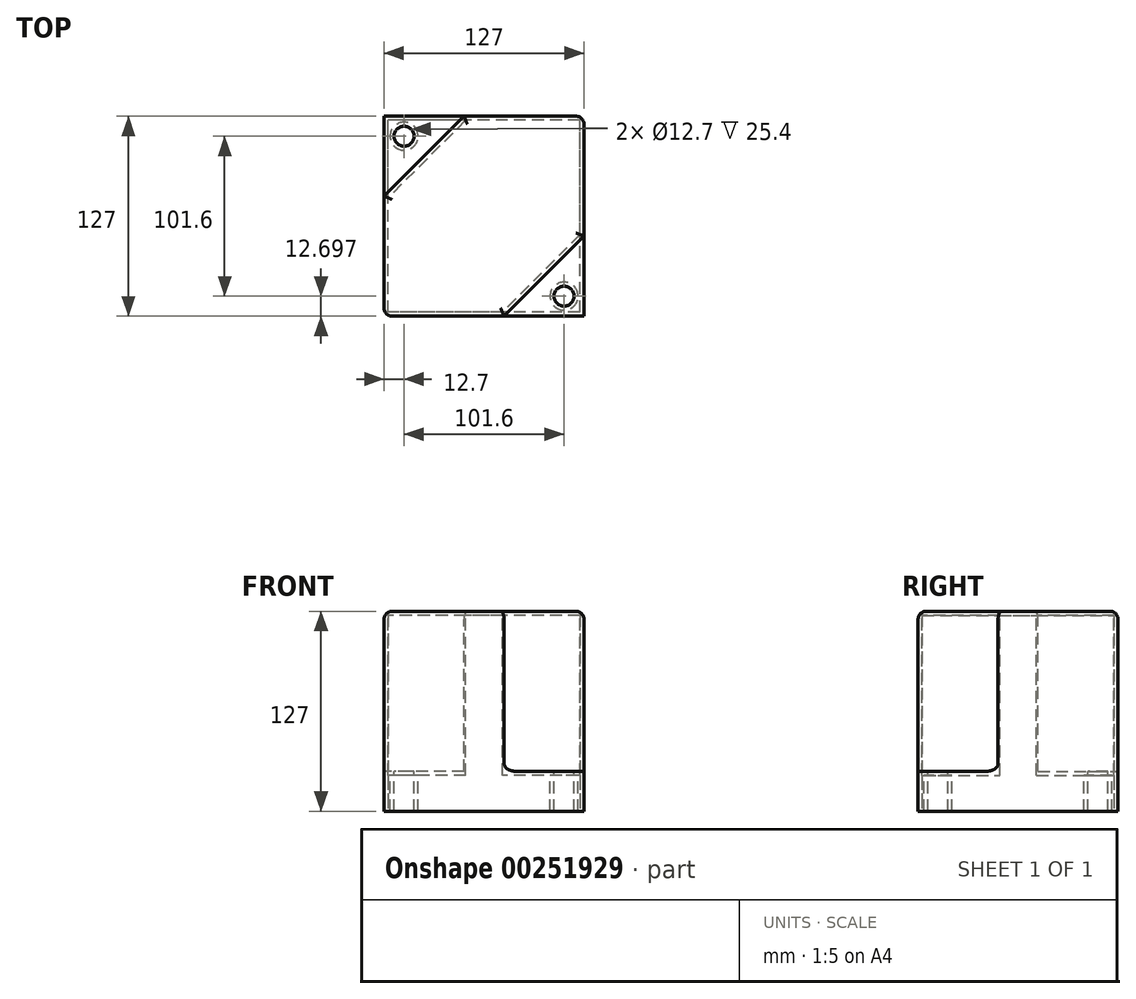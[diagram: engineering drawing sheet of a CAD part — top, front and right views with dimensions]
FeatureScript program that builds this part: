
annotation { "Feature Type Name" : "Feature", "Feature Type Description" : "" }
export const myFeature = defineFeature(function(context is Context, id is Id, definition is map)
    precondition{}
    {
        {
            var Q0;
            Q0=qCreatedBy(makeId("Top.planeOp"),FACE);
            var sketch = newSketch(context, id + "F0", { "sketchPlane" : qUnion([Q0])});
            skLineSegment(sketch, "E0.bottom", {"start": v(63.5, -63.6) * mm, "end": v(-63.5, -63.6) * mm});
            skLineSegment(sketch, "E0.top", {"start": v(63.5, 63.4) * mm, "end": v(-63.5, 63.4) * mm});
            skLineSegment(sketch, "E0.left", {"start": v(63.5, -63.6) * mm, "end": v(63.5, 63.4) * mm});
            skLineSegment(sketch, "E0.right", {"start": v(-63.5, -63.6) * mm, "end": v(-63.5, 63.4) * mm});
            skPoint(sketch, "E0.middle", {"position": v(0, -0.1) * mm});
            skSolve(sketch);
        }
        {
            var Q0;
            Q0 = qSketchRegion(id + "F0", true);
            extrude(context, id + "F1", {"entities" : qUnion([Q0]), "depth" : 127 * mm});
        }
        {
            var Q0;
            Q0=makeQuery(id+"F1.opExtrude","CAP_FACE",FACE,{"disambiguationData":[OSD([sQuery(id+"F0.wireOp",EDGE,"E0.bottom"),sQuery(id+"F0.wireOp",EDGE,"E0.top"),sQuery(id+"F0.wireOp",EDGE,"E0.left"),sQuery(id+"F0.wireOp",EDGE,"E0.right")])],"isStart":false});
            var sketch = newSketch(context, id + "F2", { "sketchPlane" : qUnion([Q0])});
            skLineSegment(sketch, "E1", {"start": v(-63.5, 63.4) * mm, "end": v(-12.7, 63.4) * mm});
            skLineSegment(sketch, "E2", {"start": v(-12.7, 63.4) * mm, "end": v(-63.5, 12.6) * mm});
            skLineSegment(sketch, "E3", {"start": v(-63.5, 12.6) * mm, "end": v(-63.5, 63.4) * mm});
            skLineSegment(sketch, "E4", {"start": v(63.5, -63.6) * mm, "end": v(63.5, -12.8) * mm});
            skLineSegment(sketch, "E5", {"start": v(63.5, -12.8) * mm, "end": v(12.7, -63.6) * mm});
            skLineSegment(sketch, "E6", {"start": v(12.7, -63.6) * mm, "end": v(63.5, -63.6) * mm});
            skSolve(sketch);
        }
        {
            var Q0;
            Q0=makeQuery(id+"F2.imprint","IMPRINT",FACE,{"disambiguationData":[TD([[makeQuery(id+"F2.imprint","IMPRINT",EDGE,{"derivedFrom":sQuery(id+"F2.wireOp",EDGE,"E1")}),1.0]])]});
            var Q1;
            Q1=makeQuery(id+"F2.imprint","IMPRINT",FACE,{"disambiguationData":[TD([[makeQuery(id+"F2.imprint","IMPRINT",EDGE,{"derivedFrom":sQuery(id+"F2.wireOp",EDGE,"E4")}),1.0]])]});
            extrude(context, id + "F3", {"entities" : qUnion([Q0, Q1]), "operationType" : NewBodyOperationType.REMOVE, "oppositeDirection" : true, "depth" : 101.6 * mm});
        }
        {
            var Q0;
            Q0=makeQuery(id+"F1.opExtrude","CAP_FACE",FACE,{"disambiguationData":[OSD([sQuery(id+"F0.wireOp",EDGE,"E0.bottom"),sQuery(id+"F0.wireOp",EDGE,"E0.top"),sQuery(id+"F0.wireOp",EDGE,"E0.left"),sQuery(id+"F0.wireOp",EDGE,"E0.right")])],"isStart":false});
            var sketch = newSketch(context, id + "F4", { "sketchPlane" : qUnion([Q0])});
            skCircle(sketch, "E7", {"center": v(-50.8, 50.7) * mm, "radius": 6.35 * mm});
            skCircle(sketch, "E8", {"center": v(50.8, -50.9) * mm, "radius": 6.35 * mm});
            skSolve(sketch);
        }
        {
            var Q0;
            Q0=makeQuery(id+"F4.imprint","IMPRINT",FACE,{"disambiguationData":[TD([[makeQuery(id+"F4.imprint","IMPRINT",EDGE,{"derivedFrom":sQuery(id+"F4.wireOp",EDGE,"E7")}),1.0]])]});
            var Q1;
            Q1=makeQuery(id+"F4.imprint","IMPRINT",FACE,{"disambiguationData":[TD([[makeQuery(id+"F4.imprint","IMPRINT",EDGE,{"derivedFrom":sQuery(id+"F4.wireOp",EDGE,"E8")}),1.0]])]});
            extrude(context, id + "F5", {"entities" : qUnion([Q0, Q1]), "operationType" : NewBodyOperationType.REMOVE, "oppositeDirection" : true, "depth" : 203.2 * mm});
        }
        {
            var Q0;
            Q0=makeQuery(id+"F1.opExtrude","CAP_FACE",FACE,{"disambiguationData":[OSD([sQuery(id+"F0.wireOp",EDGE,"E0.bottom"),sQuery(id+"F0.wireOp",EDGE,"E0.top"),sQuery(id+"F0.wireOp",EDGE,"E0.left"),sQuery(id+"F0.wireOp",EDGE,"E0.right")])],"isStart":true});
            shell(context, id + "F6", {"entities" : qUnion([Q0]), "thickness" : 2.54 * mm});
        }
        {
            var Q0;
            Q0=makeQuery(id+"F3.boolean.opBoolean","COPY",EDGE,{"derivedFrom":makeQuery(id+"F3.opExtrude","CAP_EDGE",EDGE,{"disambiguationData":[OSD([sQuery(id+"F2.wireOp",EDGE,"E5")])],"isStart":true})});
            var Q1;
            Q1=makeQuery(id+"F1.opExtrude","CAP_EDGE",EDGE,{"disambiguationData":[OSD([sQuery(id+"F0.wireOp",EDGE,"E0.bottom")])],"isStart":false});
            var Q2;
            Q2=makeQuery(id+"F1.opExtrude","CAP_EDGE",EDGE,{"disambiguationData":[OSD([sQuery(id+"F0.wireOp",EDGE,"E0.right")])],"isStart":false});
            var Q3;
            Q3=makeQuery(id+"F1.opExtrude","CAP_FACE",FACE,{"disambiguationData":[OSD([sQuery(id+"F0.wireOp",EDGE,"E0.bottom"),sQuery(id+"F0.wireOp",EDGE,"E0.top"),sQuery(id+"F0.wireOp",EDGE,"E0.left"),sQuery(id+"F0.wireOp",EDGE,"E0.right")])],"isStart":false});
            var Q4;
            Q4=makeQuery(id+"F3.boolean.opBoolean","COPY",EDGE,{"derivedFrom":makeQuery(id+"F3.opExtrude","SWEPT_EDGE",EDGE,{"disambiguationData":[OSD([sQuery(id+"F0.wireOp",EDGE,"E0.left"),sQuery(id+"F2.wireOp",EDGE,"E4"),sQuery(id+"F2.wireOp",EDGE,"E5")])]})});
            var Q5;
            Q5=makeQuery(id+"F3.boolean.opBoolean","COPY",EDGE,{"derivedFrom":makeQuery(id+"F3.opExtrude","SWEPT_EDGE",EDGE,{"disambiguationData":[OSD([sQuery(id+"F0.wireOp",EDGE,"E0.bottom"),sQuery(id+"F2.wireOp",EDGE,"E5"),sQuery(id+"F2.wireOp",EDGE,"E6")])]})});
            var Q6;
            Q6=makeQuery(id+"F3.boolean.opBoolean","COPY",EDGE,{"derivedFrom":makeQuery(id+"F3.opExtrude","CAP_EDGE",EDGE,{"disambiguationData":[OSD([sQuery(id+"F2.wireOp",EDGE,"E6")])],"isStart":false})});
            var Q7;
            Q7=makeQuery(id+"F3.boolean.opBoolean","COPY",EDGE,{"derivedFrom":makeQuery(id+"F3.opExtrude","CAP_EDGE",EDGE,{"disambiguationData":[OSD([sQuery(id+"F2.wireOp",EDGE,"E4")])],"isStart":false})});
            var Q8;
            Q8=makeQuery(id+"F3.boolean.opBoolean","COPY",EDGE,{"derivedFrom":makeQuery(id+"F3.opExtrude","CAP_EDGE",EDGE,{"disambiguationData":[OSD([sQuery(id+"F2.wireOp",EDGE,"E5")])],"isStart":false})});
            var Q9;
            Q9=makeQuery(id+"F1.opExtrude","SWEPT_EDGE",EDGE,{"disambiguationData":[OSD([sQuery(id+"F0.wireOp",EDGE,"E0.top"),sQuery(id+"F0.wireOp",EDGE,"E0.left")])]});
            var Q10;
            Q10=makeQuery(id+"F1.opExtrude","SWEPT_EDGE",EDGE,{"disambiguationData":[OSD([sQuery(id+"F0.wireOp",EDGE,"E0.bottom"),sQuery(id+"F0.wireOp",EDGE,"E0.right")])]});
            var Q11;
            Q11=makeQuery(id+"F3.boolean.opBoolean","COPY",EDGE,{"derivedFrom":makeQuery(id+"F3.opExtrude","SWEPT_EDGE",EDGE,{"disambiguationData":[OSD([sQuery(id+"F0.wireOp",EDGE,"E0.top"),sQuery(id+"F2.wireOp",EDGE,"E1"),sQuery(id+"F2.wireOp",EDGE,"E2")])]})});
            var Q12;
            Q12=makeQuery(id+"F3.boolean.opBoolean","COPY",EDGE,{"derivedFrom":makeQuery(id+"F3.opExtrude","SWEPT_EDGE",EDGE,{"disambiguationData":[OSD([sQuery(id+"F0.wireOp",EDGE,"E0.right"),sQuery(id+"F2.wireOp",EDGE,"E2"),sQuery(id+"F2.wireOp",EDGE,"E3")])]})});
            var Q13;
            Q13=makeQuery(id+"F3.boolean.opBoolean","COPY",EDGE,{"derivedFrom":makeQuery(id+"F3.opExtrude","CAP_EDGE",EDGE,{"disambiguationData":[OSD([sQuery(id+"F2.wireOp",EDGE,"E3")])],"isStart":false})});
            var Q14;
            Q14=makeQuery(id+"F3.boolean.opBoolean","COPY",EDGE,{"derivedFrom":makeQuery(id+"F3.opExtrude","CAP_EDGE",EDGE,{"disambiguationData":[OSD([sQuery(id+"F2.wireOp",EDGE,"E1")])],"isStart":false})});
            fillet(context, id + "F7", {"entities" : qUnion([Q0, Q1, Q2, Q3, Q4, Q5, Q6, Q7, Q8, Q9, Q10, Q11, Q12, Q13, Q14]), "radius" : 5.08 * mm, "tangentPropagation" : true, "allowEdgeOverflow" : false});
        }
    });
